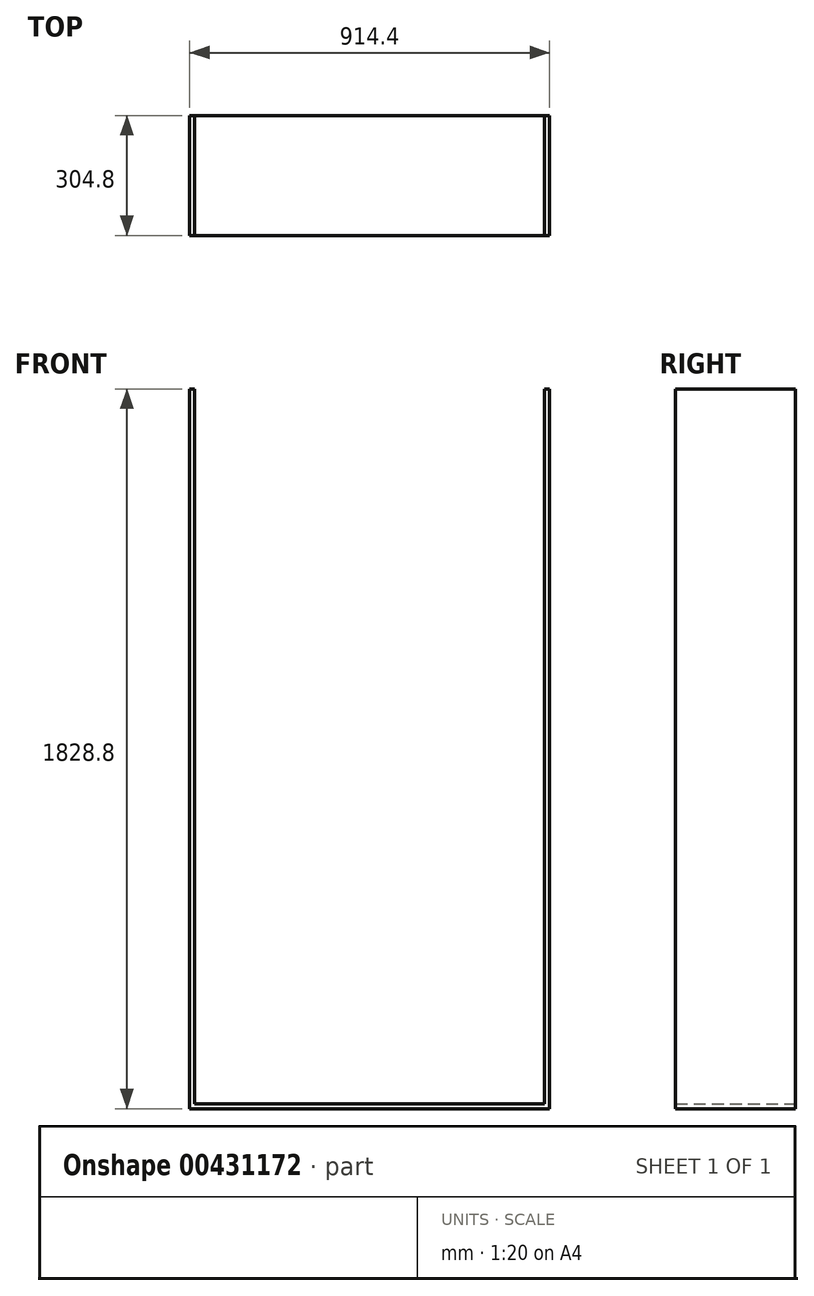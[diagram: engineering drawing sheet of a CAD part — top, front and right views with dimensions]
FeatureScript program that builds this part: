
annotation { "Feature Type Name" : "Feature", "Feature Type Description" : "" }
export const myFeature = defineFeature(function(context is Context, id is Id, definition is map)
    precondition{}
    {
        {
            var Q0;
            Q0=qCreatedBy(makeId("Front.planeOp"),FACE);
            var sketch = newSketch(context, id + "F0", { "sketchPlane" : qUnion([Q0])});
            skLineSegment(sketch, "E0.right", {"start": v(282.54, 901.7) * mm, "end": v(282.54, 469.9) * mm});
            skLineSegment(sketch, "E1.bottom", {"start": v(-606.46, -215.9) * mm, "end": v(282.54, -215.9) * mm});
            skLineSegment(sketch, "E1.top", {"start": v(-606.46, -927.1) * mm, "end": v(282.54, -927.1) * mm});
            skLineSegment(sketch, "E2.top", {"start": v(-225.46, -215.9) * mm, "end": v(282.54, -215.9) * mm});
            skLineSegment(sketch, "E2.left", {"start": v(-225.46, 469.9) * mm, "end": v(-225.46, -215.9) * mm});
            skLineSegment(sketch, "E2.right", {"start": v(282.54, 469.9) * mm, "end": v(282.54, -215.9) * mm});
            skLineSegment(sketch, "E3.top", {"start": v(-606.46, 901.7) * mm, "end": v(282.54, 901.7) * mm});
            skLineSegment(sketch, "E3.left", {"start": v(-606.46, -215.9) * mm, "end": v(-606.46, 901.7) * mm});
            skLineSegment(sketch, "E3.right", {"start": v(282.54, -215.9) * mm, "end": v(282.54, 901.7) * mm});
            skLineSegment(sketch, "E4.bottom", {"start": v(-225.46, -215.9) * mm, "end": v(-606.46, -215.9) * mm});
            skLineSegment(sketch, "E4.left", {"start": v(-225.46, -215.9) * mm, "end": v(-225.46, 469.9) * mm});
            skLineSegment(sketch, "E4.right", {"start": v(-606.46, -215.9) * mm, "end": v(-606.46, 469.9) * mm});
            skLineSegment(sketch, "E5.top", {"start": v(-606.46, -215.9) * mm, "end": v(-225.46, -215.9) * mm});
            skLineSegment(sketch, "E5.left", {"start": v(-606.46, 469.9) * mm, "end": v(-606.46, -215.9) * mm});
            skLineSegment(sketch, "E6.bottom", {"start": v(-200.06, 393.7) * mm, "end": v(257.14, 393.7) * mm});
            skLineSegment(sketch, "E6.top", {"start": v(-200.06, -215.9) * mm, "end": v(257.14, -215.9) * mm});
            skLineSegment(sketch, "E6.left", {"start": v(-200.06, 393.7) * mm, "end": v(-200.06, -215.9) * mm});
            skLineSegment(sketch, "E6.right", {"start": v(257.14, 393.7) * mm, "end": v(257.14, -215.9) * mm});
            skLineSegment(sketch, "E7", {"start": v(257.14, 294.85) * mm, "end": v(282.54, 294.85) * mm, "construction": true});
            skLineSegment(sketch, "E8", {"start": v(-225.46, 277.66) * mm, "end": v(-200.06, 277.66) * mm, "construction": true});
            skLineSegment(sketch, "E9", {"start": v(-606.46, -215.9) * mm, "end": v(-606.46, -927.1) * mm});
            skLineSegment(sketch, "E10", {"start": v(282.54, -215.9) * mm, "end": v(282.54, -927.1) * mm});
            skLineSegment(sketch, "E11.top", {"start": v(-606.46, -914.4) * mm, "end": v(282.54, -914.4) * mm});
            skLineSegment(sketch, "E11.left", {"start": v(-606.46, -927.1) * mm, "end": v(-606.46, -914.4) * mm});
            skLineSegment(sketch, "E11.right", {"start": v(282.54, -927.1) * mm, "end": v(282.54, -914.4) * mm});
            skLineSegment(sketch, "E12.top", {"start": v(-606.46, -228.6) * mm, "end": v(282.54, -228.6) * mm});
            skLineSegment(sketch, "E12.left", {"start": v(-606.46, -215.9) * mm, "end": v(-606.46, -228.6) * mm});
            skLineSegment(sketch, "E12.right", {"start": v(282.54, -215.9) * mm, "end": v(282.54, -228.6) * mm});
            skLineSegment(sketch, "E13.bottom", {"start": v(282.54, 901.7) * mm, "end": v(295.24, 901.7) * mm});
            skLineSegment(sketch, "E13.top", {"start": v(282.54, -927.1) * mm, "end": v(295.24, -927.1) * mm});
            skLineSegment(sketch, "E13.left", {"start": v(282.54, 901.7) * mm, "end": v(282.54, -927.1) * mm});
            skLineSegment(sketch, "E13.right", {"start": v(295.24, 901.7) * mm, "end": v(295.24, -927.1) * mm});
            skLineSegment(sketch, "E14.bottom", {"start": v(-606.46, 901.7) * mm, "end": v(-619.16, 901.7) * mm});
            skLineSegment(sketch, "E14.top", {"start": v(-606.46, -927.1) * mm, "end": v(-619.16, -927.1) * mm});
            skLineSegment(sketch, "E14.left", {"start": v(-606.46, 901.7) * mm, "end": v(-606.46, -927.1) * mm});
            skLineSegment(sketch, "E14.right", {"start": v(-619.16, 901.7) * mm, "end": v(-619.16, -927.1) * mm});
            skLineSegment(sketch, "E15.top", {"start": v(-606.46, 889) * mm, "end": v(282.54, 889) * mm});
            skLineSegment(sketch, "E15.left", {"start": v(-606.46, 901.7) * mm, "end": v(-606.46, 889) * mm});
            skLineSegment(sketch, "E15.right", {"start": v(282.54, 901.7) * mm, "end": v(282.54, 889) * mm});
            skLineSegment(sketch, "E16.top", {"start": v(-225.46, -215.9) * mm, "end": v(-238.16, -215.9) * mm});
            skLineSegment(sketch, "E16.right", {"start": v(-238.16, 469.9) * mm, "end": v(-238.16, -215.9) * mm});
            skLineSegment(sketch, "E17.top", {"start": v(-606.46, -406.4) * mm, "end": v(282.54, -406.4) * mm});
            skLineSegment(sketch, "E17.left", {"start": v(-606.46, -228.6) * mm, "end": v(-606.46, -406.4) * mm});
            skLineSegment(sketch, "E17.right", {"start": v(282.54, -228.6) * mm, "end": v(282.54, -406.4) * mm});
            skLineSegment(sketch, "E18.top", {"start": v(-606.46, -419.1) * mm, "end": v(282.54, -419.1) * mm});
            skLineSegment(sketch, "E18.left", {"start": v(-606.46, -406.4) * mm, "end": v(-606.46, -419.1) * mm});
            skLineSegment(sketch, "E18.right", {"start": v(282.54, -406.4) * mm, "end": v(282.54, -419.1) * mm});
            skLineSegment(sketch, "E19.top", {"start": v(-606.46, -596.9) * mm, "end": v(282.54, -596.9) * mm});
            skLineSegment(sketch, "E19.left", {"start": v(-606.46, -419.1) * mm, "end": v(-606.46, -596.9) * mm});
            skLineSegment(sketch, "E19.right", {"start": v(282.54, -419.1) * mm, "end": v(282.54, -596.9) * mm});
            skLineSegment(sketch, "E20.top", {"start": v(-606.46, -609.6) * mm, "end": v(282.54, -609.6) * mm});
            skLineSegment(sketch, "E20.left", {"start": v(-606.46, -596.9) * mm, "end": v(-606.46, -609.6) * mm});
            skLineSegment(sketch, "E20.right", {"start": v(282.54, -596.9) * mm, "end": v(282.54, -609.6) * mm});
            skLineSegment(sketch, "E21.top", {"start": v(-606.46, 406.4) * mm, "end": v(-238.16, 406.4) * mm});
            skLineSegment(sketch, "E21.left", {"start": v(-606.46, 482.6) * mm, "end": v(-606.46, 406.4) * mm});
            skLineSegment(sketch, "E21.right", {"start": v(-238.16, 469.9) * mm, "end": v(-238.16, 406.4) * mm});
            skLineSegment(sketch, "E22.top", {"start": v(-606.46, 393.7) * mm, "end": v(-238.16, 393.7) * mm});
            skLineSegment(sketch, "E22.left", {"start": v(-606.46, 406.4) * mm, "end": v(-606.46, 393.7) * mm});
            skLineSegment(sketch, "E22.right", {"start": v(-238.16, 406.4) * mm, "end": v(-238.16, 393.7) * mm});
            skLineSegment(sketch, "E23.top", {"start": v(-606.46, 317.5) * mm, "end": v(-238.16, 317.5) * mm});
            skLineSegment(sketch, "E23.left", {"start": v(-606.46, 393.7) * mm, "end": v(-606.46, 317.5) * mm});
            skLineSegment(sketch, "E23.right", {"start": v(-238.16, 393.7) * mm, "end": v(-238.16, 317.5) * mm});
            skLineSegment(sketch, "E24.top", {"start": v(-606.46, 304.8) * mm, "end": v(-238.16, 304.8) * mm});
            skLineSegment(sketch, "E24.left", {"start": v(-606.46, 317.5) * mm, "end": v(-606.46, 304.8) * mm});
            skLineSegment(sketch, "E24.right", {"start": v(-238.16, 317.5) * mm, "end": v(-238.16, 304.8) * mm});
            skLineSegment(sketch, "E25.top", {"start": v(-606.46, 228.6) * mm, "end": v(-238.16, 228.6) * mm});
            skLineSegment(sketch, "E25.left", {"start": v(-606.46, 304.8) * mm, "end": v(-606.46, 228.6) * mm});
            skLineSegment(sketch, "E25.right", {"start": v(-238.16, 304.8) * mm, "end": v(-238.16, 228.6) * mm});
            skLineSegment(sketch, "E26.top", {"start": v(-606.46, 215.9) * mm, "end": v(-238.16, 215.9) * mm});
            skLineSegment(sketch, "E26.left", {"start": v(-606.46, 228.6) * mm, "end": v(-606.46, 215.9) * mm});
            skLineSegment(sketch, "E26.right", {"start": v(-238.16, 228.6) * mm, "end": v(-238.16, 215.9) * mm});
            skLineSegment(sketch, "E27.top", {"start": v(-606.46, 88.9) * mm, "end": v(-238.16, 88.9) * mm});
            skLineSegment(sketch, "E27.left", {"start": v(-606.46, 215.9) * mm, "end": v(-606.46, 88.9) * mm});
            skLineSegment(sketch, "E27.right", {"start": v(-238.16, 215.9) * mm, "end": v(-238.16, 88.9) * mm});
            skLineSegment(sketch, "E28.top", {"start": v(-606.46, 76.2) * mm, "end": v(-238.16, 76.2) * mm});
            skLineSegment(sketch, "E28.left", {"start": v(-606.46, 88.9) * mm, "end": v(-606.46, 76.2) * mm});
            skLineSegment(sketch, "E28.right", {"start": v(-238.16, 88.9) * mm, "end": v(-238.16, 76.2) * mm});
            skLineSegment(sketch, "E29.top", {"start": v(-606.46, -50.8) * mm, "end": v(-238.16, -50.8) * mm});
            skLineSegment(sketch, "E29.left", {"start": v(-606.46, 76.2) * mm, "end": v(-606.46, -50.8) * mm});
            skLineSegment(sketch, "E29.right", {"start": v(-238.16, 76.2) * mm, "end": v(-238.16, -50.8) * mm});
            skLineSegment(sketch, "E30.top", {"start": v(-606.46, -63.5) * mm, "end": v(-238.16, -63.5) * mm});
            skLineSegment(sketch, "E30.left", {"start": v(-606.46, -50.8) * mm, "end": v(-606.46, -63.5) * mm});
            skLineSegment(sketch, "E30.right", {"start": v(-238.16, -50.8) * mm, "end": v(-238.16, -63.5) * mm});
            skLineSegment(sketch, "E31", {"start": v(-238.16, 469.9) * mm, "end": v(-225.46, 469.9) * mm});
            skLineSegment(sketch, "E32.bottom", {"start": v(-606.46, 482.6) * mm, "end": v(282.54, 482.6) * mm});
            skLineSegment(sketch, "E32.top", {"start": v(-606.46, 469.9) * mm, "end": v(282.54, 469.9) * mm});
            skLineSegment(sketch, "E32.left", {"start": v(-606.46, 482.6) * mm, "end": v(-606.46, 469.9) * mm});
            skLineSegment(sketch, "E32.right", {"start": v(282.54, 482.6) * mm, "end": v(282.54, 469.9) * mm});
            skSolve(sketch);
        }
        {
            var Q0;
            Q0=makeQuery(id+"F0.imprint","IMPRINT",FACE,{"disambiguationData":[TD([[makeQuery(id+"F0.imprint","IMPRINT",EDGE,{"derivedFrom":sQuery(id+"F0.wireOp",EDGE,"E3.top")}),-1.0]])]});
            var Q1;
            Q1=makeQuery(id+"F0.imprint","IMPRINT",FACE,{"disambiguationData":[TD([[makeQuery(id+"F0.imprint","IMPRINT",EDGE,{"derivedFrom":sQuery(id+"F0.wireOp",EDGE,"E14.bottom")}),1.0]])]});
            var Q2;
            Q2=makeQuery(id+"F0.imprint","IMPRINT",FACE,{"disambiguationData":[TD([[makeQuery(id+"F0.imprint","IMPRINT",EDGE,{"derivedFrom":sQuery(id+"F0.wireOp",EDGE,"E13.bottom")}),-1.0]])]});
            var Q3;
            {var subQ0=sQuery(id+"F0.wireOp",EDGE,"E1.top");Q3=makeQuery(id+"F0.imprint","IMPRINT",FACE,{"disambiguationData":[TD([[makeQuery(id+"F0.imprint","IMPRINT",EDGE,{"derivedFrom":subQ0}),1.0]])]});}
            var Q4;
            {var subQ5=sQuery(id+"F0.wireOp",EDGE,"E16.top");Q4=makeQuery(id+"F0.imprint","IMPRINT",FACE,{"disambiguationData":[TD([[makeQuery(id+"F0.imprint","IMPRINT",EDGE,{"derivedFrom":subQ5}),1.0]])]});}
            extrude(context, id + "F1", {"entities" : qUnion([Q0, Q1, Q2, Q3, Q4]), "depth" : 304.8 * mm});
        }
    });
